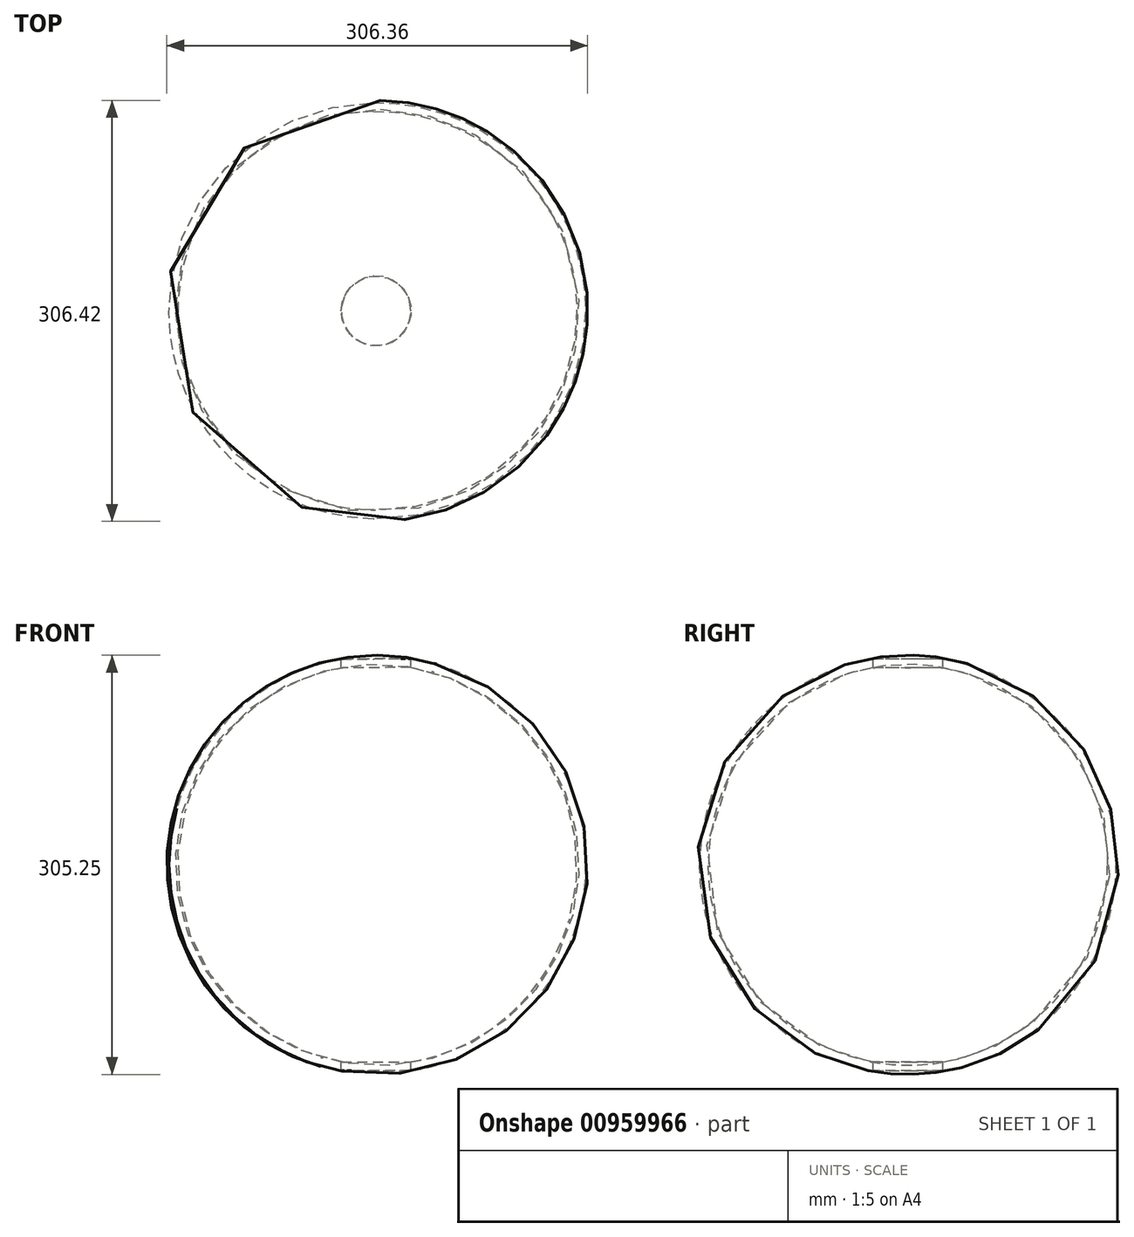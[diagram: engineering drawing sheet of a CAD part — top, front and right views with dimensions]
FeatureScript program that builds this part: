
annotation { "Feature Type Name" : "Feature", "Feature Type Description" : "" }
export const myFeature = defineFeature(function(context is Context, id is Id, definition is map)
    precondition{}
    {
        {
            var Q0;
            Q0=qCreatedBy(makeId("Front.planeOp"),FACE);
            var sketch = newSketch(context, id + "F0", { "sketchPlane" : qUnion([Q0])});
            skCircle(sketch, "E0", {"center": v(0, 0) * mm, "radius": 152.4 * mm});
            skCircle(sketch, "E1.0", {"center": v(0, 0) * mm, "radius": 146.05 * mm});
            skLineSegment(sketch, "E2", {"start": v(-41.5, -146.64) * mm, "end": v(43.05, 146.2) * mm});
            skSolve(sketch);
        }
        {
            var Q0;
            {var subQ0=sQuery(id+"F0.wireOp",EDGE,"E2");var subQ1=sQuery(id+"F0.wireOp",EDGE,"E0");var subQ2=makeQuery(id+"F0.imprint","INTERSECT",VERTEX,{"disambiguationData":[OD(0.0)],"derivedFrom":[subQ1,subQ0]});Q0=makeQuery(id+"F0.imprint","IMPRINT",FACE,{"disambiguationData":[TD([[makeQuery(id+"F0.imprint","IMPRINT",EDGE,{"disambiguationData":[TD([[subQ2,1.0]])],"derivedFrom":subQ1}),1.0]])]});}
            var Q1;
            Q1=sQuery(id+"F0.wireOp",EDGE,"E2");
            revolve(context, id + "F1", {"surfaceOperationType" : NewSurfaceOperationType.NEW, "entities" : qUnion([Q0]), "axis" : qUnion([Q1]), "revolveType" : RevolveType.ONE_DIRECTION, "angle" : 180 * degree});
        }
        {
            var Q0;
            Q0=qCreatedBy(makeId("Top.planeOp"),FACE);
            var sketch = newSketch(context, id + "F2", { "sketchPlane" : qUnion([Q0])});
            skCircle(sketch, "E3", {"center": v(0, 0) * mm, "radius": 25.4 * mm});
            skSolve(sketch);
        }
        {
            var Q0;
            Q0=makeQuery(id+"F2.imprint","IMPRINT",FACE,{"disambiguationData":[TD([[makeQuery(id+"F2.imprint","IMPRINT",EDGE,{"derivedFrom":sQuery(id+"F2.wireOp",EDGE,"E3")}),1.0]])]});
            extrude(context, id + "F3", {"entities" : qUnion([Q0]), "operationType" : NewBodyOperationType.REMOVE, "oppositeDirection" : true, "depth" : 304.8 * mm, "offsetDistance" : 25.4 * mm, "hasSecondDirection" : true, "secondDirectionOppositeDirection" : false, "secondDirectionDepth" : 304.8 * mm});
        }
        {
            var Q0;
            Q0=makeQuery(id+"F1.opRevolve","SWEPT_BODY",BODY,{"disambiguationData":[OSD([sQuery(id+"F0.wireOp",EDGE,"E0"),sQuery(id+"F0.wireOp",EDGE,"E1.0"),sQuery(id+"F0.wireOp",EDGE,"E2")])]});
            var Q1;
            Q1=makeQuery(id+"F3.boolean.opBoolean","SPLIT",FACE,{"disambiguationData":[OD(1.0)],"derivedFrom":makeQuery(id+"F1.opRevolve","CAP_FACE",FACE,{"disambiguationData":[OSD([sQuery(id+"F0.wireOp",EDGE,"E0"),sQuery(id+"F0.wireOp",EDGE,"E1.0"),sQuery(id+"F0.wireOp",EDGE,"E2")])],"isStart":true})});
            mirror(context, id + "F4", {"operationType" : NewBodyOperationType.ADD, "entities" : qUnion([Q0]), "mirrorPlane" : qUnion([Q1])});
        }
    });
